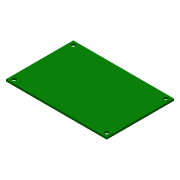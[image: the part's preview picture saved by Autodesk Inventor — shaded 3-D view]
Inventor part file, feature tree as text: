
AUTODESK INVENTOR PART (.ipt)
format: ipt  version: 2013 (Build 170138000, 138)  size: 87,552 bytes
history: native  units: in
note: dims shown in document units (in); Inventor stores cm internally (conversion verified against a paired STEP export)
features: extrude x2, sketch x2
ambient origin geometry x8: Origin, YZ Plane, XZ Plane, XY Plane, X Axis, Y Axis, Z Axis, Center Point
bodies: Solid1 (feature_tree)
feature tree (4):
  extrude  "Extrusion1"  Depth=2.01in
  extrude  "Extrusion2"  Depth=0.12in
  sketch  "Sketch1"  dims[d0=3.01in d1=2.01in]
  sketch  "Sketch2"  dims[d2=0.06in d3=0.0in d4=0.12in d5=0.12in d6=0.12in d7=0.12in d8=0.12in d9=0.12in d10=0.12in d11=0.12in d12=0.12in d13=1.0in d14=0.0in]
